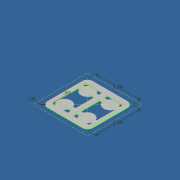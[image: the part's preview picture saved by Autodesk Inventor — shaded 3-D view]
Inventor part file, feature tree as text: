
AUTODESK INVENTOR PART (.ipt)
format: ipt  version: 2016 (Build 200138000, 138)  size: 168,448 bytes
history: native  units: in
note: dims shown in document units (in); Inventor stores cm internally (conversion verified against a paired STEP export)
features: extrude x2, sketch x2, other x1
ambient origin geometry x8: Origin, YZ Plane, XZ Plane, XY Plane, X Axis, Y Axis, Z Axis, Center Point
bodies: Solid1 (feature_tree), Solid2 (feature_tree)
feature tree (5):
  extrude  "Extrusion1"  Depth=1.2in
  extrude  "Extrusion2"  Depth=0.1in
  sketch  "Sketch1"  dims[d15=1.2in d16=1.2in]
  other  "Image3"
  sketch  "Sketch2"  dims[d17=0.138in d21=0.1in d22=0.009in d23=0.0in d24=0.35in d25=0.3in d26=1.5748in d28=360.0deg d30=0.013in d31=-0.5909in]
